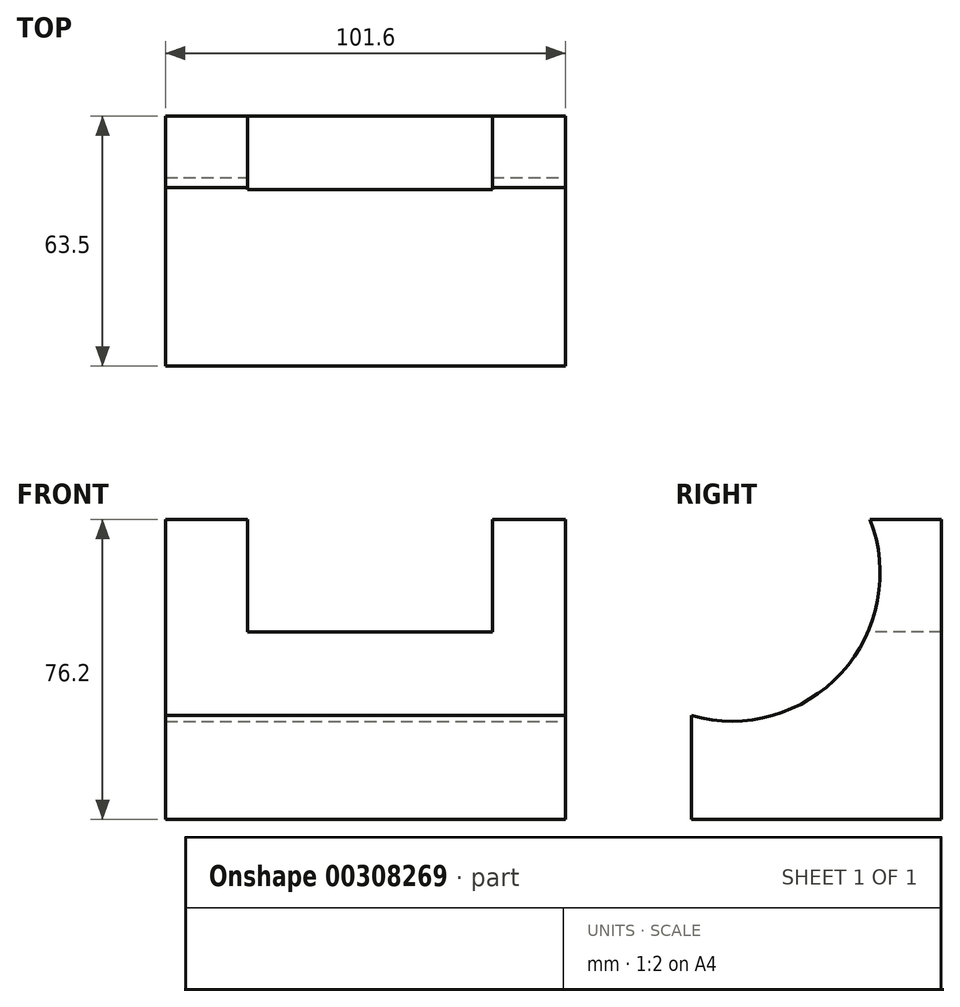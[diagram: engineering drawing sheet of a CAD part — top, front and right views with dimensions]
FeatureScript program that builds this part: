
annotation { "Feature Type Name" : "Feature", "Feature Type Description" : "" }
export const myFeature = defineFeature(function(context is Context, id is Id, definition is map)
    precondition{}
    {
        {
            var Q0;
            Q0=qCreatedBy(makeId("Front.planeOp"),FACE);
            var sketch = newSketch(context, id + "F0", { "sketchPlane" : qUnion([Q0])});
            skLineSegment(sketch, "E0", {"start": v(-94.39, -47.64) * mm, "end": v(7.21, -47.64) * mm});
            skLineSegment(sketch, "E1", {"start": v(7.21, -47.64) * mm, "end": v(7.21, -22.24) * mm});
            skLineSegment(sketch, "E2", {"start": v(7.21, -22.24) * mm, "end": v(-94.39, -22.24) * mm});
            skLineSegment(sketch, "E3", {"start": v(-94.39, -22.24) * mm, "end": v(-94.39, -47.64) * mm});
            skLineSegment(sketch, "E4", {"start": v(-94.39, -22.24) * mm, "end": v(-94.39, 28.56) * mm});
            skLineSegment(sketch, "E5", {"start": v(-94.39, 28.56) * mm, "end": v(7.21, 28.56) * mm});
            skLineSegment(sketch, "E6", {"start": v(7.21, 28.56) * mm, "end": v(7.21, -22.24) * mm});
            skSolve(sketch);
        }
        {
            var Q0;
            Q0=makeQuery(id+"F0.imprint","IMPRINT",FACE,{"disambiguationData":[TD([[makeQuery(id+"F0.imprint","IMPRINT",EDGE,{"derivedFrom":sQuery(id+"F0.wireOp",EDGE,"E0")}),1.0]])]});
            var Q1;
            Q1=makeQuery(id+"F0.imprint","IMPRINT",FACE,{"disambiguationData":[TD([[makeQuery(id+"F0.imprint","IMPRINT",EDGE,{"derivedFrom":sQuery(id+"F0.wireOp",EDGE,"E2")}),-1.0]])]});
            extrude(context, id + "F1", {"entities" : qUnion([Q0, Q1]), "oppositeDirection" : true, "depth" : 63.5 * mm});
        }
        {
            var Q0;
            Q0=qCreatedBy(makeId("Right.planeOp"),FACE);
            var sketch = newSketch(context, id + "F2", { "sketchPlane" : qUnion([Q0])});
            skCircle(sketch, "E7", {"center": v(10.27, 14.98) * mm, "radius": 37.65 * mm});
            skSolve(sketch);
        }
        {
            var Q0;
            Q0=makeQuery(id+"F2.imprint","IMPRINT",FACE,{"disambiguationData":[TD([[makeQuery(id+"F2.imprint","IMPRINT",EDGE,{"derivedFrom":sQuery(id+"F2.wireOp",EDGE,"E7")}),1.0]])]});
            extrude(context, id + "F3", {"entities" : qUnion([Q0]), "operationType" : NewBodyOperationType.REMOVE, "oppositeDirection" : true, "depth" : 101.6 * mm});
        }
        {
            var Q0;
            Q0=makeQuery(id+"F3.boolean.opBoolean","COPY",FACE,{"derivedFrom":makeQuery(id+"F3.opExtrude","CAP_FACE",FACE,{"disambiguationData":[OSD([sQuery(id+"F2.wireOp",EDGE,"E7")])],"isStart":true})});
            extrude(context, id + "F4", {"entities" : qUnion([Q0]), "operationType" : NewBodyOperationType.REMOVE, "oppositeDirection" : true, "depth" : 25.4 * mm});
        }
        {
            var Q0;
            Q0=qCreatedBy(makeId("Front.planeOp"),FACE);
            var sketch = newSketch(context, id + "F5", { "sketchPlane" : qUnion([Q0])});
            skLineSegment(sketch, "E8", {"start": v(-73.56, 28.95) * mm, "end": v(-73.56, 0) * mm});
            skLineSegment(sketch, "E9", {"start": v(-73.56, 0) * mm, "end": v(-11.38, 0) * mm});
            skLineSegment(sketch, "E10", {"start": v(-11.38, 0) * mm, "end": v(-11.38, 28.95) * mm});
            skLineSegment(sketch, "E11", {"start": v(-11.38, 28.95) * mm, "end": v(-73.56, 28.95) * mm});
            skSolve(sketch);
        }
        {
            var Q0;
            Q0 = qSketchRegion(id + "F5", true);
            extrude(context, id + "F6", {"entities" : qUnion([Q0]), "operationType" : NewBodyOperationType.REMOVE, "oppositeDirection" : true, "depth" : 127 * mm});
        }
    });
